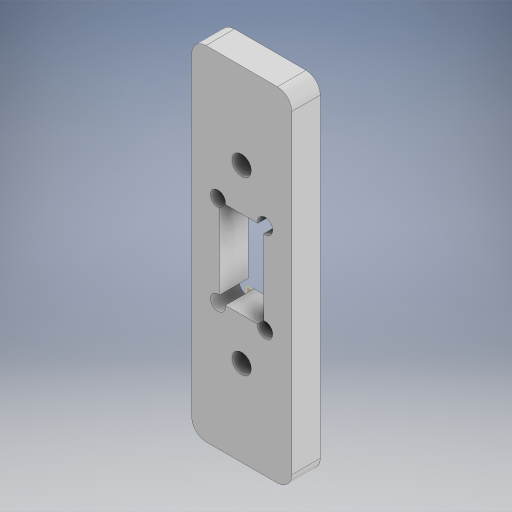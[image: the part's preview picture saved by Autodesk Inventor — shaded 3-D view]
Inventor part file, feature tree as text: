
AUTODESK INVENTOR PART (.ipt)
format: ipt  version: 2024 (Build 280153000, 153)  size: 333,824 bytes
history: native  units: mm
features: other x6, sketch x3, reference x3, extrude x2, projected_geometry x2, fillet x1, hole x1
ambient origin geometry x8: Origin, YZ Plane, XZ Plane, XY Plane, X Axis, Y Axis, Z Axis, Center Point
bodies: Body1 (feature_tree)
feature tree (18):
  other  "솔리드1"
  other  "작업 평면1"
  extrude  "돌출1"  Depth=0.3mm
  fillet  "모깎기1"  Radius=2.1mm
  extrude  "돌출2"  Depth=2.1mm
  hole  "구멍1"  [1 undecoded]
  sketch  "스케치1"
  reference  "참조1"
  reference  "참조2"
  reference  "참조3"
  sketch  "스케치2"
  projected_geometry  "투영된 루프1"
  sketch  "스케치3"
  projected_geometry  "투영된 루프2"
  other  "<userpath>\Desktop\ZIG\조립품1.iam"
  other  "조립품1.iam"
  other  "arm_attack_conn:1"
  other  "조립품1"
note: 1 required parameter value undecoded (feature->parameter linkage not recoverable at this tier; creation-order binding heuristic only, values carry confidence <= 0.55)
